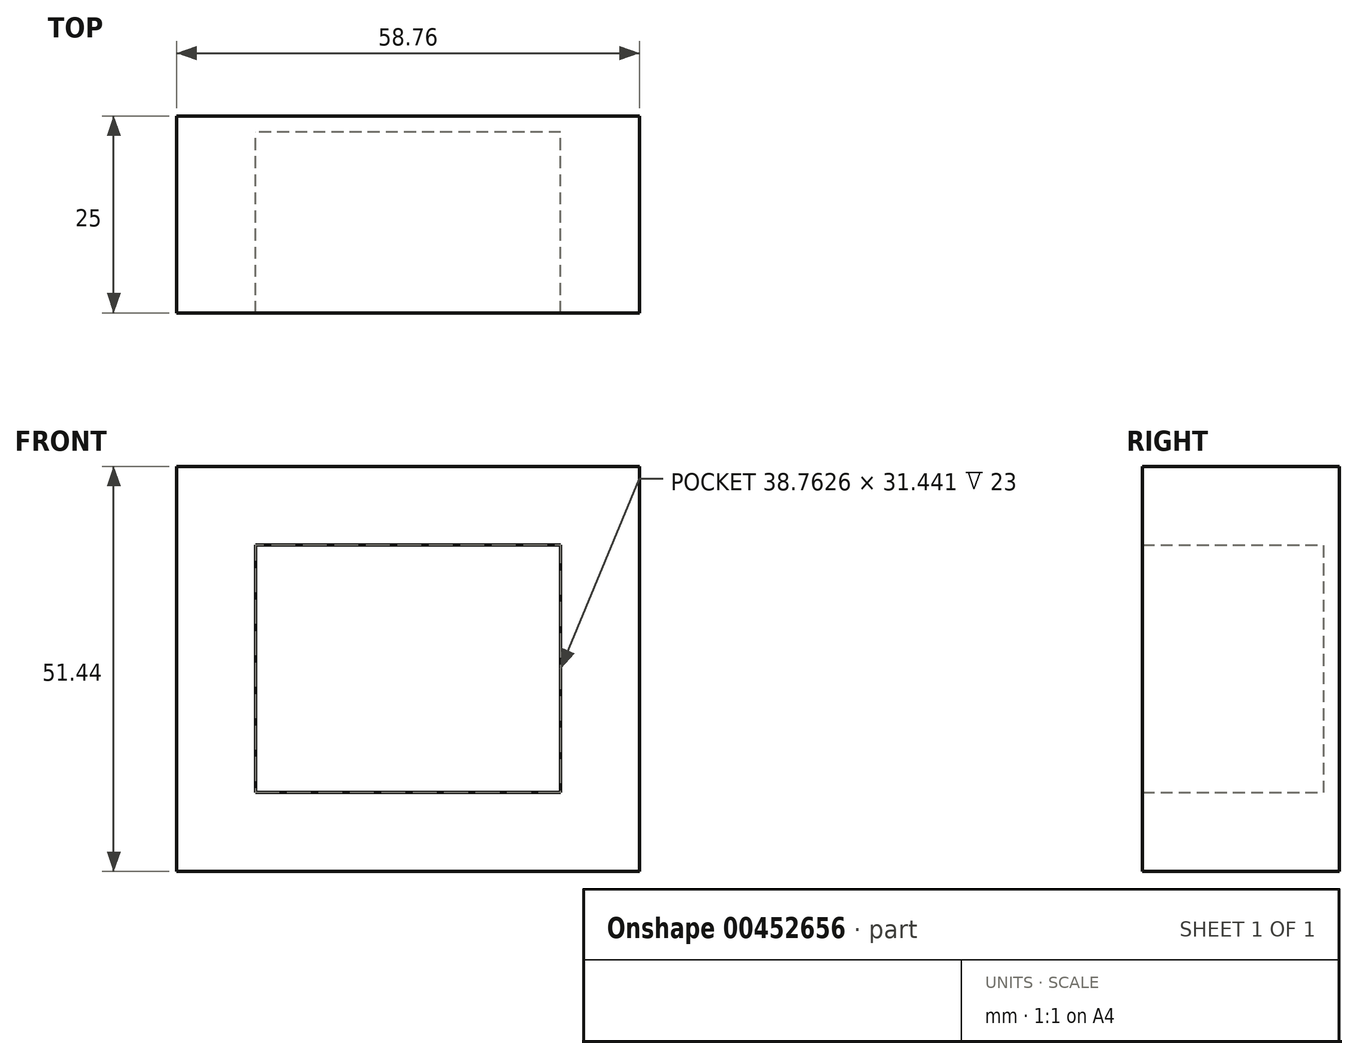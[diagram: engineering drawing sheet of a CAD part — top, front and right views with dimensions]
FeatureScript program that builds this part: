
annotation { "Feature Type Name" : "Feature", "Feature Type Description" : "" }
export const myFeature = defineFeature(function(context is Context, id is Id, definition is map)
    precondition{}
    {
        {
            var Q0;
            Q0=qCreatedBy(makeId("Front.planeOp"),FACE);
            var sketch = newSketch(context, id + "F0", { "sketchPlane" : qUnion([Q0])});
            skLineSegment(sketch, "E0.bottom", {"start": v(19.38, -15.72) * mm, "end": v(-19.38, -15.72) * mm});
            skLineSegment(sketch, "E0.top", {"start": v(19.38, 15.72) * mm, "end": v(-19.38, 15.72) * mm});
            skLineSegment(sketch, "E0.left", {"start": v(19.38, -15.72) * mm, "end": v(19.38, 15.72) * mm});
            skLineSegment(sketch, "E0.right", {"start": v(-19.38, -15.72) * mm, "end": v(-19.38, 15.72) * mm});
            skPoint(sketch, "E0.middle", {"position": v(0, 0) * mm});
            skLineSegment(sketch, "E1.0", {"start": v(29.38, 25.72) * mm, "end": v(-29.38, 25.72) * mm});
            skLineSegment(sketch, "E1.1", {"start": v(29.38, -25.72) * mm, "end": v(29.38, 25.72) * mm});
            skLineSegment(sketch, "E1.2", {"start": v(29.38, -25.72) * mm, "end": v(-29.38, -25.72) * mm});
            skLineSegment(sketch, "E1.3", {"start": v(-29.38, -25.72) * mm, "end": v(-29.38, 25.72) * mm});
            skSolve(sketch);
        }
        {
            var Q0;
            Q0=makeQuery(id+"F0.imprint","IMPRINT",FACE,{"disambiguationData":[TD([[makeQuery(id+"F0.imprint","IMPRINT",EDGE,{"derivedFrom":sQuery(id+"F0.wireOp",EDGE,"E0.bottom")}),1.0]])]});
            var sketch = newSketch(context, id + "F1", { "sketchPlane" : qUnion([Q0])});
            skSolve(sketch);
        }
        {
            var Q0;
            Q0=makeQuery(id+"F1.imprint","IMPRINT",FACE,{"disambiguationData":[TD([[makeQuery(id+"F1.imprint","IMPRINT",EDGE,{"derivedFrom":makeQuery(id+"F0.imprint","IMPRINT",EDGE,{"derivedFrom":sQuery(id+"F0.wireOp",EDGE,"E0.bottom")})}),1.0]])]});
            extrude(context, id + "F2", {"entities" : qUnion([Q0]), "depth" : 25 * mm});
        }
        {
            var Q0;
            Q0 = qSketchRegion(id + "F0", true);
            var Q1;
            Q1=makeQuery(id+"F1.imprint","IMPRINT",FACE,{"disambiguationData":[TD([[makeQuery(id+"F1.imprint","IMPRINT",EDGE,{"derivedFrom":makeQuery(id+"F0.imprint","IMPRINT",EDGE,{"derivedFrom":sQuery(id+"F0.wireOp",EDGE,"E0.bottom")})}),-1.0]])]});
            extrude(context, id + "F3", {"entities" : qUnion([Q0, Q1]), "operationType" : NewBodyOperationType.ADD, "depth" : 2 * mm});
        }
    });
